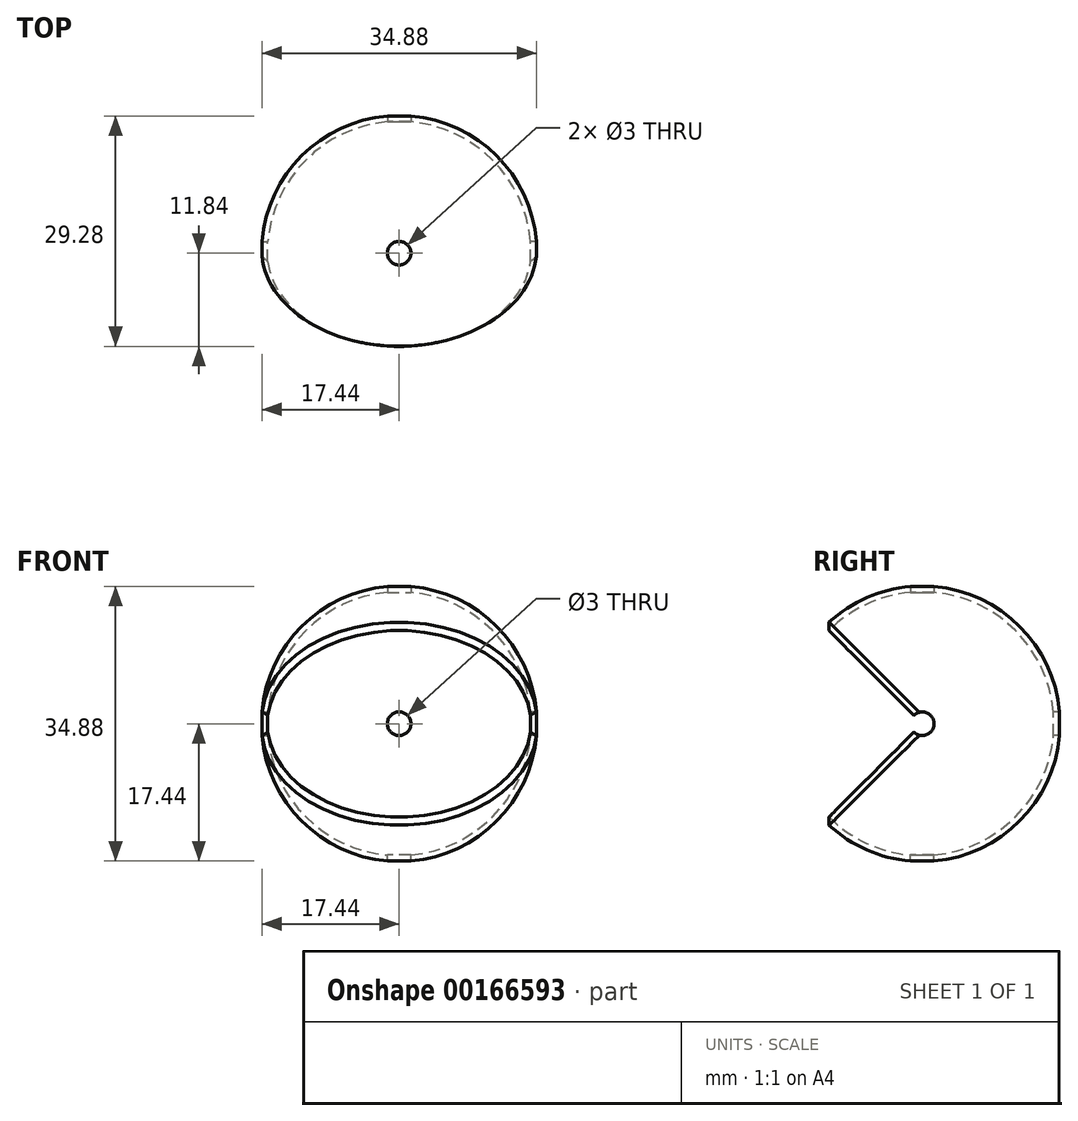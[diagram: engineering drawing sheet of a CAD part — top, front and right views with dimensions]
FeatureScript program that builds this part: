
annotation { "Feature Type Name" : "Feature", "Feature Type Description" : "" }
export const myFeature = defineFeature(function(context is Context, id is Id, definition is map)
    precondition{}
    {
        {
            var Q0;
            Q0=qCreatedBy(makeId("Top.planeOp"),FACE);
            var sketch = newSketch(context, id + "F0", { "sketchPlane" : qUnion([Q0])});
            skLineSegment(sketch, "E0", {"start": v(-20.58, 0) * mm, "end": v(21.91, 0) * mm});
            skArc(sketch, "E1", {"start": v(17.5, 0) * mm, "mid": v(0, 17.5) * mm, "end": v(-17.5, 0) * mm});
            skSolve(sketch);
        }
        {
            var Q0;
            {var subQ0=sQuery(id+"F0.wireOp",EDGE,"E1");Q0=makeQuery(id+"F0.imprint","IMPRINT",FACE,{"disambiguationData":[TD([[makeQuery(id+"F0.imprint","IMPRINT",EDGE,{"derivedFrom":subQ0}),1.0]])]});}
            var Q1;
            Q1=sQuery(id+"F0.wireOp",EDGE,"E0");
            revolve(context, id + "F1", {"entities" : qUnion([Q0]), "axis" : qUnion([Q1]), "revolveType" : RevolveType.ONE_DIRECTION, "angle" : 270 * degree});
        }
        {
            var Q0;
            Q0=makeQuery(id+"F1.opRevolve","CAP_FACE",FACE,{"disambiguationData":[OSD([sQuery(id+"F0.wireOp",EDGE,"E0"),sQuery(id+"F0.wireOp",EDGE,"E1")])],"isStart":true});
            var Q1;
            Q1=makeQuery(id+"F1.opRevolve","CAP_FACE",FACE,{"disambiguationData":[OSD([sQuery(id+"F0.wireOp",EDGE,"E0"),sQuery(id+"F0.wireOp",EDGE,"E1")])],"isStart":false});
            var Q2;
            Q2=makeQuery(id+"F1.opRevolve","SWEPT_BODY",BODY,{"disambiguationData":[OSD([sQuery(id+"F0.wireOp",EDGE,"E0"),sQuery(id+"F0.wireOp",EDGE,"E1")])]});
            shell(context, id + "F15", {"entities" : qUnion([Q0, Q1]), "parts" : qUnion([Q2]), "thickness" : .75 * mm});
        }
        {
            var Q0;
            Q0=qCreatedBy(makeId("Right.planeOp"),FACE);
            var sketch = newSketch(context, id + "F2", { "sketchPlane" : qUnion([Q0])});
            skPoint(sketch, "E2", {"position": v(0, 0) * mm});
            skSolve(sketch);
        }
        {
            var Q0;
            Q0=sQuery(id+"F2.wireOp",VERTEX,"E2");
            var Q1;
            Q1=makeQuery(id+"F1.opRevolve","SWEPT_BODY",BODY,{"disambiguationData":[OSD([sQuery(id+"F0.wireOp",EDGE,"E0"),sQuery(id+"F0.wireOp",EDGE,"E1")])]});
            hole(context, id + "F3", {"style" : HoleStyle.SIMPLE, "endStyle" : HoleEndStyle.THROUGH, "holeDiameter" : 3 * mm, "locations" : qUnion([Q0]), "scope" : qUnion([Q1]), "isTappedThrough" : true});
        }
        {
            var Q0;
            Q0=qCreatedBy(makeId("Right.planeOp"),FACE);
            var sketch = newSketch(context, id + "F4", { "sketchPlane" : qUnion([Q0])});
            skPoint(sketch, "E3", {"position": v(0, 0) * mm});
            skSolve(sketch);
        }
        {
            var Q0;
            Q0=sQuery(id+"F4.wireOp",VERTEX,"E3");
            var Q1;
            Q1=makeQuery(id+"F1.opRevolve","SWEPT_BODY",BODY,{"disambiguationData":[OSD([sQuery(id+"F0.wireOp",EDGE,"E0"),sQuery(id+"F0.wireOp",EDGE,"E1")])]});
            hole(context, id + "F5", {"style" : HoleStyle.SIMPLE, "endStyle" : HoleEndStyle.THROUGH, "oppositeDirection" : true, "holeDiameter" : 3 * mm, "locations" : qUnion([Q0]), "scope" : qUnion([Q1]), "isTappedThrough" : true});
        }
        {
            var Q0;
            Q0=qCreatedBy(makeId("Top.planeOp"),FACE);
            var sketch = newSketch(context, id + "F6", { "sketchPlane" : qUnion([Q0])});
            skLineSegment(sketch, "E4", {"start": v(20, 0) * mm, "end": v(-20, 0) * mm});
            skPoint(sketch, "E5", {"position": v(17.06, 1.5) * mm});
            skPoint(sketch, "E6", {"position": v(-17.06, 1.5) * mm});
            skPoint(sketch, "E7", {"position": v(0, 0) * mm});
            skSolve(sketch);
        }
        {
            var Q0;
            Q0=makeQuery(id+"F1.opRevolve","SWEPT_BODY",BODY,{"disambiguationData":[OSD([sQuery(id+"F0.wireOp",EDGE,"E0"),sQuery(id+"F0.wireOp",EDGE,"E1")])]});
            var Q1;
            Q1=sQuery(id+"F6.wireOp",EDGE,"E4");
            var Q2;
            Q2=sQuery(id+"F6.wireOp",EDGE,"E4");
            transform(context, id + "F7", {"entities" : qUnion([Q0]), "transformType" : TransformType.ROTATION, "transformAxis" : qUnion([Q2]), "angle" : 135 * degree, "makeCopy" : false});
        }
        {
            var Q0;
            Q0=qCreatedBy(makeId("Front.planeOp"),FACE);
            var sketch = newSketch(context, id + "F8", { "sketchPlane" : qUnion([Q0])});
            skPoint(sketch, "E8", {"position": v(0, 0) * mm});
            skSolve(sketch);
        }
        {
            var Q0;
            Q0=sQuery(id+"F8.wireOp",VERTEX,"E8");
            var Q1;
            Q1=makeQuery(id+"F1.opRevolve","SWEPT_BODY",BODY,{"disambiguationData":[OSD([sQuery(id+"F0.wireOp",EDGE,"E0"),sQuery(id+"F0.wireOp",EDGE,"E1")])]});
            hole(context, id + "F9", {"style" : HoleStyle.SIMPLE, "endStyle" : HoleEndStyle.THROUGH, "holeDiameter" : 3 * mm, "locations" : qUnion([Q0]), "scope" : qUnion([Q1]), "isTappedThrough" : true});
        }
        {
            var Q0;
            Q0=qCreatedBy(makeId("Top.planeOp"),FACE);
            var sketch = newSketch(context, id + "F10", { "sketchPlane" : qUnion([Q0])});
            skPoint(sketch, "E9", {"position": v(0, 0) * mm});
            skSolve(sketch);
        }
        {
            var Q0;
            Q0=sQuery(id+"F10.wireOp",VERTEX,"E9");
            var Q1;
            Q1=makeQuery(id+"F1.opRevolve","SWEPT_BODY",BODY,{"disambiguationData":[OSD([sQuery(id+"F0.wireOp",EDGE,"E0"),sQuery(id+"F0.wireOp",EDGE,"E1")])]});
            hole(context, id + "F11", {"style" : HoleStyle.SIMPLE, "endStyle" : HoleEndStyle.THROUGH, "holeDiameter" : 3 * mm, "locations" : qUnion([Q0]), "scope" : qUnion([Q1]), "isTappedThrough" : true});
        }
        {
            var Q0;
            Q0=qCreatedBy(makeId("Top.planeOp"),FACE);
            var sketch = newSketch(context, id + "F12", { "sketchPlane" : qUnion([Q0])});
            skPoint(sketch, "E10", {"position": v(0, 0) * mm});
            skSolve(sketch);
        }
        {
            var Q0;
            Q0=sQuery(id+"F12.wireOp",VERTEX,"E10");
            var Q1;
            Q1=makeQuery(id+"F1.opRevolve","SWEPT_BODY",BODY,{"disambiguationData":[OSD([sQuery(id+"F0.wireOp",EDGE,"E0"),sQuery(id+"F0.wireOp",EDGE,"E1")])]});
            hole(context, id + "F13", {"style" : HoleStyle.SIMPLE, "endStyle" : HoleEndStyle.THROUGH, "oppositeDirection" : true, "holeDiameter" : 3 * mm, "locations" : qUnion([Q0]), "scope" : qUnion([Q1]), "isTappedThrough" : true});
        }
        {
            var Q0;
            Q0=makeQuery(id+"F1.opRevolve","CAP_EDGE",EDGE,{"disambiguationData":[OSD([sQuery(id+"F0.wireOp",EDGE,"E1")])],"isStart":false});
            var Q1;
            Q1=makeQuery(id+"F1.opRevolve","CAP_EDGE",EDGE,{"disambiguationData":[OSD([sQuery(id+"F0.wireOp",EDGE,"E1")])],"isStart":true});
            chamfer(context, id + "F14", {"entities" : qUnion([Q0, Q1]), "width" : .735 * mm, "tangentPropagation" : true});
        }
    });
